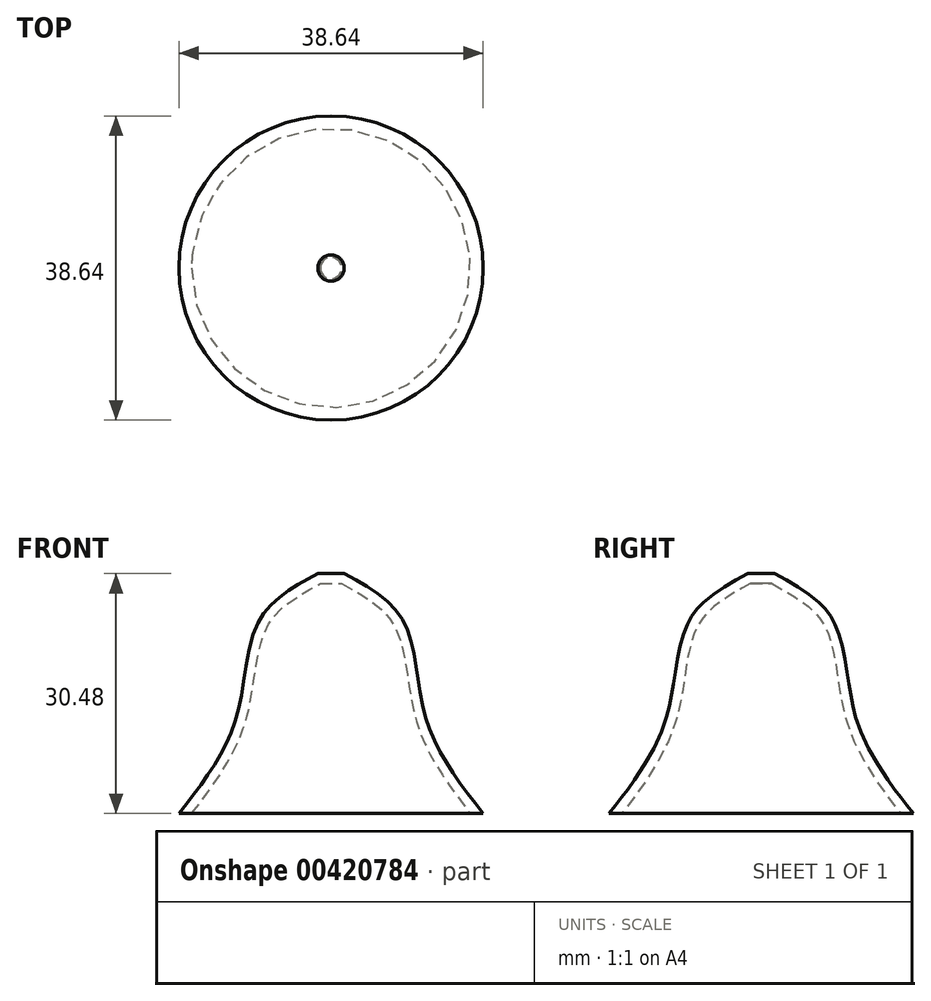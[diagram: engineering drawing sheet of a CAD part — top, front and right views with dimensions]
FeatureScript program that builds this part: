
annotation { "Feature Type Name" : "Feature", "Feature Type Description" : "" }
export const myFeature = defineFeature(function(context is Context, id is Id, definition is map)
    precondition{}
    {
        {
            var Q0;
            Q0=qCreatedBy(makeId("Top.planeOp"),FACE);
            var sketch = newSketch(context, id + "F0", { "sketchPlane" : qUnion([Q0])});
            skCircle(sketch, "E0", {"center": v(0, 0) * mm, "radius": 19.32 * mm});
            skLineSegment(sketch, "E1", {"start": v(0, 0) * mm, "end": v(-19.32, 0) * mm});
            skLineSegment(sketch, "E2", {"start": v(-19.32, 0) * mm, "end": v(19.32, 0) * mm});
            skSolve(sketch);
        }
        {
            var Q0;
            Q0=qCreatedBy(makeId("Top.planeOp"),FACE);
            cPlane(context, id + "F1", {"entities" : qUnion([Q0]), "cplaneType" : CPlaneType.OFFSET, "offset" : 12.7 * mm, "width" : 152.4 * mm, "height" : 152.4 * mm});
        }
        {
            var Q0;
            Q0=qCreatedBy(id+"F1.planeOp",FACE);
            var sketch = newSketch(context, id + "F2", { "sketchPlane" : qUnion([Q0])});
            skCircle(sketch, "E3", {"center": v(0, 0) * mm, "radius": 11.89 * mm});
            skSolve(sketch);
        }
        {
            var Q0;
            Q0=qCreatedBy(id+"F1.planeOp",FACE);
            cPlane(context, id + "F3", {"entities" : qUnion([Q0]), "cplaneType" : CPlaneType.OFFSET, "offset" : 12.7 * mm, "width" : 152.4 * mm, "height" : 152.4 * mm});
        }
        {
            var Q0;
            Q0=qCreatedBy(id+"F3.planeOp",FACE);
            var sketch = newSketch(context, id + "F4", { "sketchPlane" : qUnion([Q0])});
            skCircle(sketch, "E4", {"center": v(0, 0) * mm, "radius": 8.59 * mm});
            skSolve(sketch);
        }
        {
            var Q0;
            Q0=qCreatedBy(id+"F3.planeOp",FACE);
            cPlane(context, id + "F5", {"entities" : qUnion([Q0]), "cplaneType" : CPlaneType.OFFSET, "offset" : 5.08 * mm, "width" : 152.4 * mm, "height" : 152.4 * mm});
        }
        {
            var Q0;
            Q0=qCreatedBy(id+"F5.planeOp",FACE);
            var sketch = newSketch(context, id + "F6", { "sketchPlane" : qUnion([Q0])});
            skCircle(sketch, "E5", {"center": v(0, 0) * mm, "radius": 1.68 * mm});
            skSolve(sketch);
        }
        {
            var Q0;
            Q0 = qSketchRegion(id + "F0", true);
            var Q1;
            Q1 = qSketchRegion(id + "F2", true);
            var Q2;
            Q2 = qSketchRegion(id + "F4", true);
            var Q3;
            Q3 = qSketchRegion(id + "F6", true);
            loft(context, id + "F7", {"sheetProfilesArray" : [{ "sheetProfileEntities" : qUnion([Q0]) }, { "sheetProfileEntities" : qUnion([Q1]) }, { "sheetProfileEntities" : qUnion([Q2]) }, { "sheetProfileEntities" : qUnion([Q3]) }]});
        }
        {
            var Q0;
            Q0=makeQuery(id+"F7.opLoft","CAP_FACE",FACE,{"disambiguationData":[OSD([makeQuery(id+"F0.imprint","IMPRINT",FACE,{"disambiguationData":[TD([[makeQuery(id+"F0.imprint","IMPRINT",EDGE,{"derivedFrom":sQuery(id+"F0.wireOp",EDGE,"E0")}),1.0]])]})])],"isStart":true});
            shell(context, id + "F8", {"entities" : qUnion([Q0]), "thickness" : 1.27 * mm});
        }
    });
